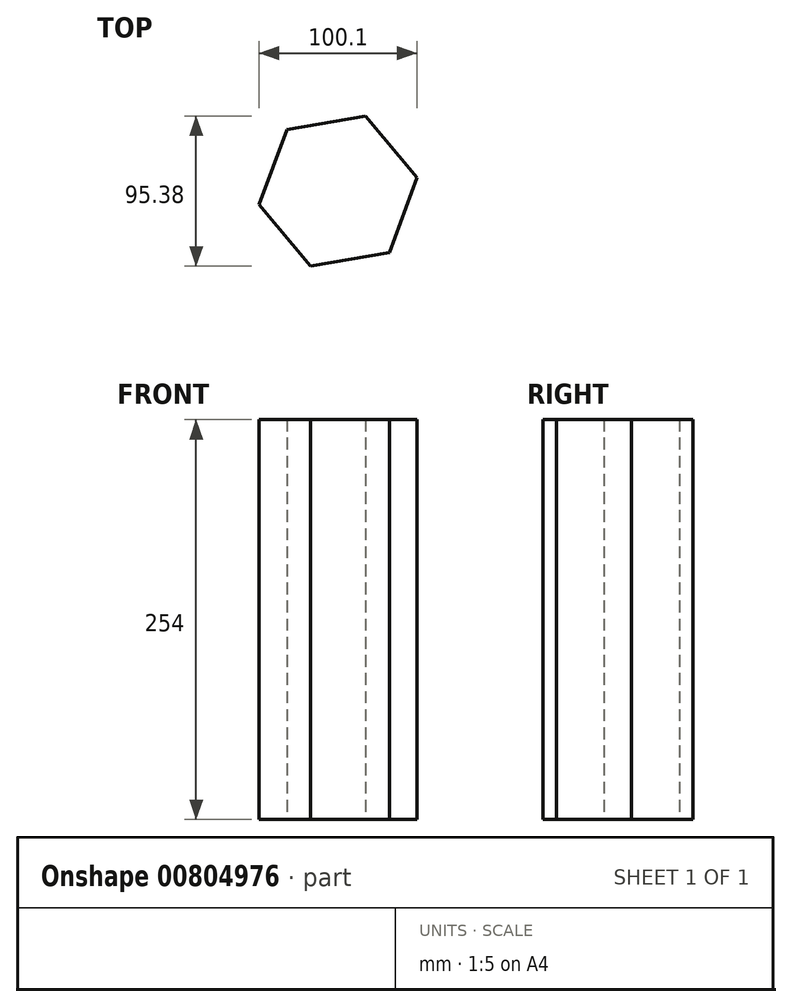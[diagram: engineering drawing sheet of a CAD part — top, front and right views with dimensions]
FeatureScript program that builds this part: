
annotation { "Feature Type Name" : "Feature", "Feature Type Description" : "" }
export const myFeature = defineFeature(function(context is Context, id is Id, definition is map)
    precondition{}
    {
        {
            var Q0;
            Q0=qCreatedBy(makeId("Top.planeOp"),FACE);
            var sketch = newSketch(context, id + "F0", { "sketchPlane" : qUnion([Q0])});
            skCircle(sketch, "E0.cCircle", {"center": v(0, 0) * mm, "radius": 44 * mm, "construction": true});
            skLineSegment(sketch, "E0.0", {"start": v(-32.56, 39) * mm, "end": v(17.49, 47.7) * mm});
            skLineSegment(sketch, "E0.1", {"start": v(17.49, 47.7) * mm, "end": v(50.05, 8.7) * mm});
            skLineSegment(sketch, "E0.2", {"start": v(50.05, 8.7) * mm, "end": v(32.56, -39) * mm});
            skLineSegment(sketch, "E0.3", {"start": v(32.56, -39) * mm, "end": v(-17.49, -47.7) * mm});
            skLineSegment(sketch, "E0.4", {"start": v(-17.49, -47.7) * mm, "end": v(-50.05, -8.7) * mm});
            skLineSegment(sketch, "E0.5", {"start": v(-50.05, -8.7) * mm, "end": v(-32.56, 39) * mm});
            skPoint(sketch, "E0.0.midPoint", {"position": v(-7.54, 43.34) * mm});
            skSolve(sketch);
        }
        {
            var Q0;
            Q0=makeQuery(id+"F0.imprint","IMPRINT",FACE,{"disambiguationData":[TD([[makeQuery(id+"F0.imprint","IMPRINT",EDGE,{"derivedFrom":sQuery(id+"F0.wireOp",EDGE,"E0.0")}),-1.0]])]});
            extrude(context, id + "F1", {"entities" : qUnion([Q0]), "depth" : 254 * mm, "offsetDistance" : 25.4 * mm});
        }
    });
